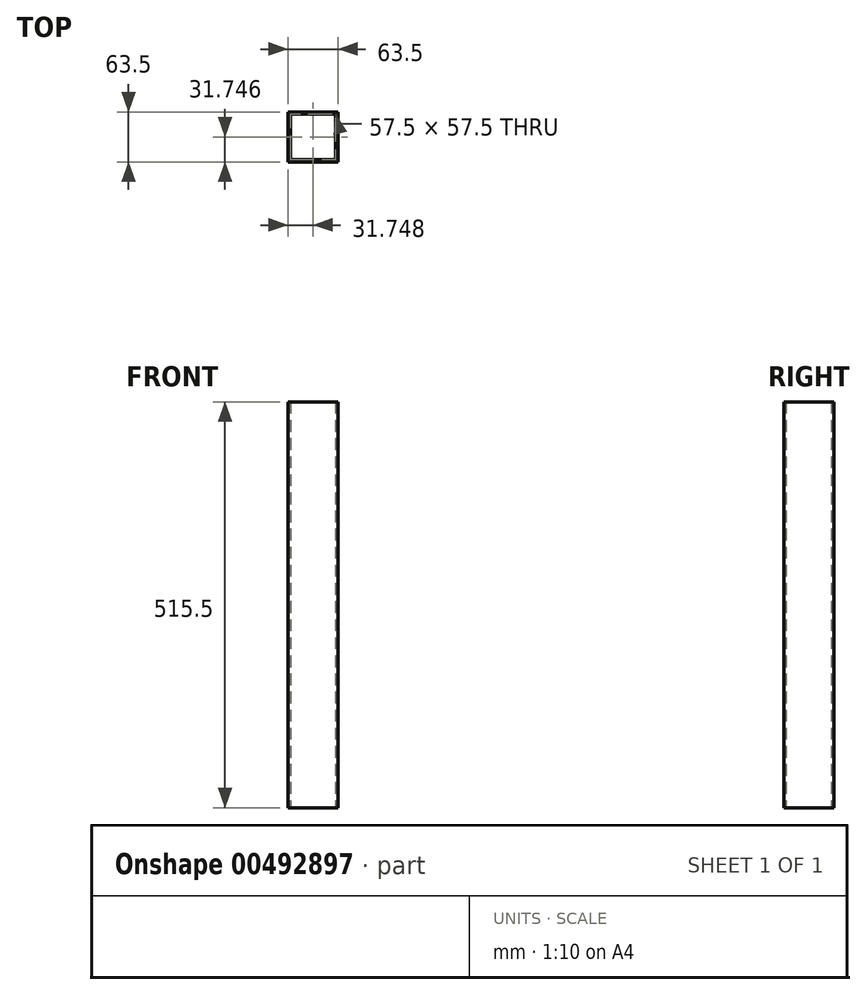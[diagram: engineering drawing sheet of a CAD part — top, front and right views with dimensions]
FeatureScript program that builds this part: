
annotation { "Feature Type Name" : "Feature", "Feature Type Description" : "" }
export const myFeature = defineFeature(function(context is Context, id is Id, definition is map)
    precondition{}
    {
        {
            var Q0;
            Q0=qCreatedBy(makeId("Top.planeOp"),FACE);
            var sketch = newSketch(context, id + "F0", { "sketchPlane" : qUnion([Q0])});
            skLineSegment(sketch, "E0.bottom", {"start": v(-28.85, 19.3) * mm, "end": v(28.65, 19.3) * mm});
            skLineSegment(sketch, "E0.top", {"start": v(-28.85, -38.2) * mm, "end": v(28.65, -38.2) * mm});
            skLineSegment(sketch, "E0.left", {"start": v(-28.85, 19.3) * mm, "end": v(-28.85, -38.2) * mm});
            skLineSegment(sketch, "E0.right", {"start": v(28.65, 19.3) * mm, "end": v(28.65, -38.2) * mm});
            skLineSegment(sketch, "E1.bottom", {"start": v(-31.85, 22.3) * mm, "end": v(31.65, 22.3) * mm});
            skLineSegment(sketch, "E1.top", {"start": v(-31.85, -41.2) * mm, "end": v(31.65, -41.2) * mm});
            skLineSegment(sketch, "E1.left", {"start": v(-31.85, 22.3) * mm, "end": v(-31.85, -41.2) * mm});
            skLineSegment(sketch, "E1.right", {"start": v(31.65, 22.3) * mm, "end": v(31.65, -41.2) * mm});
            skSolve(sketch);
        }
        {
            var Q0;
            Q0=qSketchRegion(id+"F0",true);
            extrude(context, id + "F1", {"entities" : qUnion([Q0]), "offsetDistance" : 25 * mm, "depth" : 515.5 * mm});
        }
    });
